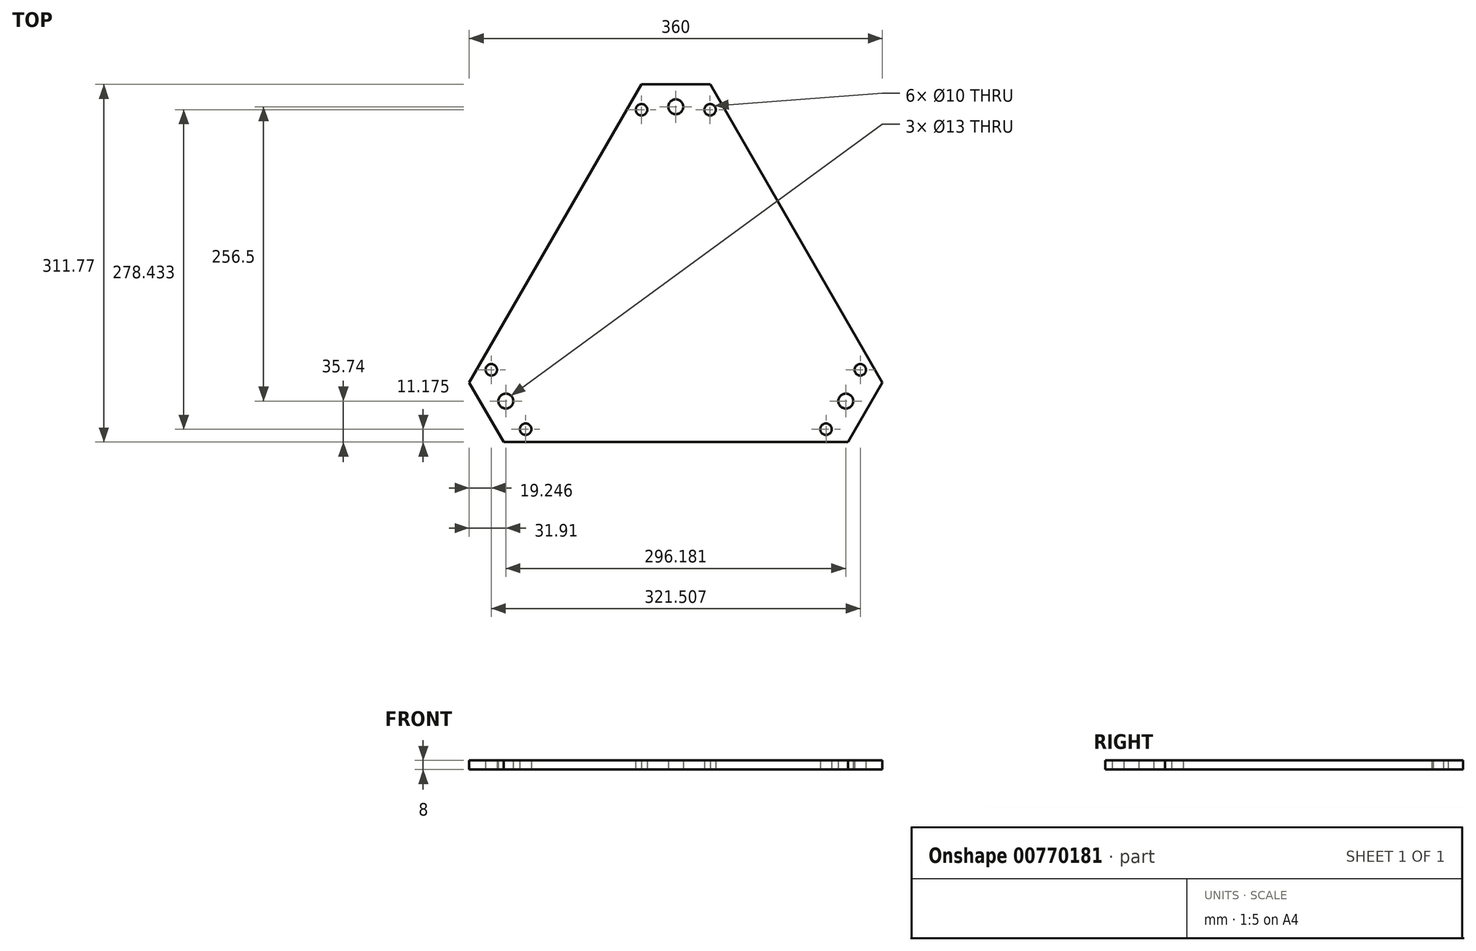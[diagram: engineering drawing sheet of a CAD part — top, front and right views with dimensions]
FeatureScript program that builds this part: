
annotation { "Feature Type Name" : "Feature", "Feature Type Description" : "" }
export const myFeature = defineFeature(function(context is Context, id is Id, definition is map)
    precondition{}
    {
        {
            var Q0;
            Q0=qCreatedBy(makeId("Top.planeOp"),FACE);
            var sketch = newSketch(context, id + "F0", { "sketchPlane" : qUnion([Q0])});
            skPoint(sketch, "E0", {"position": v(0, 0) * mm});
            skCircle(sketch, "E1", {"center": v(0, 0) * mm, "radius": 171 * mm, "construction": true});
            skLineSegment(sketch, "E2", {"start": v(0, 0) * mm, "end": v(0, 171) * mm, "construction": true});
            skLineSegment(sketch, "E3", {"start": v(0, 0) * mm, "end": v(148.1, -85.5) * mm, "construction": true});
            skLineSegment(sketch, "E4", {"start": v(0, 0) * mm, "end": v(-148.1, -85.5) * mm, "construction": true});
            skCircle(sketch, "E5", {"center": v(-148.1, -85.5) * mm, "radius": 6.5 * mm});
            skCircle(sketch, "E6", {"center": v(-160.75, -58.3) * mm, "radius": 5 * mm});
            skCircle(sketch, "E7", {"center": v(-130.87, -110.06) * mm, "radius": 5 * mm});
            skLineSegment(sketch, "E8", {"start": v(0, 0) * mm, "end": v(-160.75, -58.3) * mm, "construction": true});
            skLineSegment(sketch, "E9", {"start": v(0, 0) * mm, "end": v(-130.87, -110.06) * mm, "construction": true});
            skCircle(sketch, "E10.1.0", {"center": v(130.87, -110.06) * mm, "radius": 5 * mm});
            skCircle(sketch, "E10.1.1", {"center": v(148.1, -85.5) * mm, "radius": 6.5 * mm});
            skCircle(sketch, "E10.1.2", {"center": v(160.75, -58.3) * mm, "radius": 5 * mm});
            skLineSegment(sketch, "E10.1.3", {"start": v(0, 0) * mm, "end": v(160.75, -58.3) * mm, "construction": true});
            skLineSegment(sketch, "E10.1.5", {"start": v(0, 0) * mm, "end": v(130.87, -110.06) * mm, "construction": true});
            skCircle(sketch, "E10.2.0", {"center": v(29.88, 168.37) * mm, "radius": 5 * mm});
            skCircle(sketch, "E10.2.1", {"center": v(0, 171) * mm, "radius": 6.5 * mm});
            skCircle(sketch, "E10.2.2", {"center": v(-29.88, 168.37) * mm, "radius": 5 * mm});
            skLineSegment(sketch, "E10.2.3", {"start": v(0, 0) * mm, "end": v(-29.88, 168.37) * mm, "construction": true});
            skLineSegment(sketch, "E10.2.5", {"start": v(0, 0) * mm, "end": v(29.88, 168.37) * mm, "construction": true});
            skLineSegment(sketch, "E11", {"start": v(-180, -69.28) * mm, "end": v(-150, -121.24) * mm});
            skLineSegment(sketch, "E12", {"start": v(-150, -121.24) * mm, "end": v(150, -121.24) * mm});
            skLineSegment(sketch, "E13", {"start": v(150, -121.24) * mm, "end": v(180, -69.28) * mm});
            skLineSegment(sketch, "E14", {"start": v(180, -69.28) * mm, "end": v(30, 190.53) * mm});
            skLineSegment(sketch, "E15", {"start": v(30, 190.53) * mm, "end": v(-30, 190.53) * mm});
            skLineSegment(sketch, "E16", {"start": v(-30, 190.53) * mm, "end": v(-180, -69.28) * mm});
            skLineSegment(sketch, "E17", {"start": v(165, -95.26) * mm, "end": v(-105, 60.62) * mm, "construction": true});
            skLineSegment(sketch, "E18", {"start": v(-165, -95.26) * mm, "end": v(105, 60.62) * mm, "construction": true});
            skLineSegment(sketch, "E19", {"start": v(0, 190.53) * mm, "end": v(0, -121.24) * mm, "construction": true});
            skCircle(sketch, "E20", {"center": v(-148.1, -85.5) * mm, "radius": 30 * mm, "construction": true});
            skSolve(sketch);
        }
        {
            var Q0;
            Q0=makeQuery(id+"F0.imprint","IMPRINT",FACE,{"disambiguationData":[TD([[makeQuery(id+"F0.imprint","IMPRINT",EDGE,{"derivedFrom":sQuery(id+"F0.wireOp",EDGE,"E5")}),-1.0]])]});
            extrude(context, id + "F1", {"entities" : qUnion([Q0]), "depth" : 8 * mm, "offsetDistance" : 25 * mm});
        }
    });
